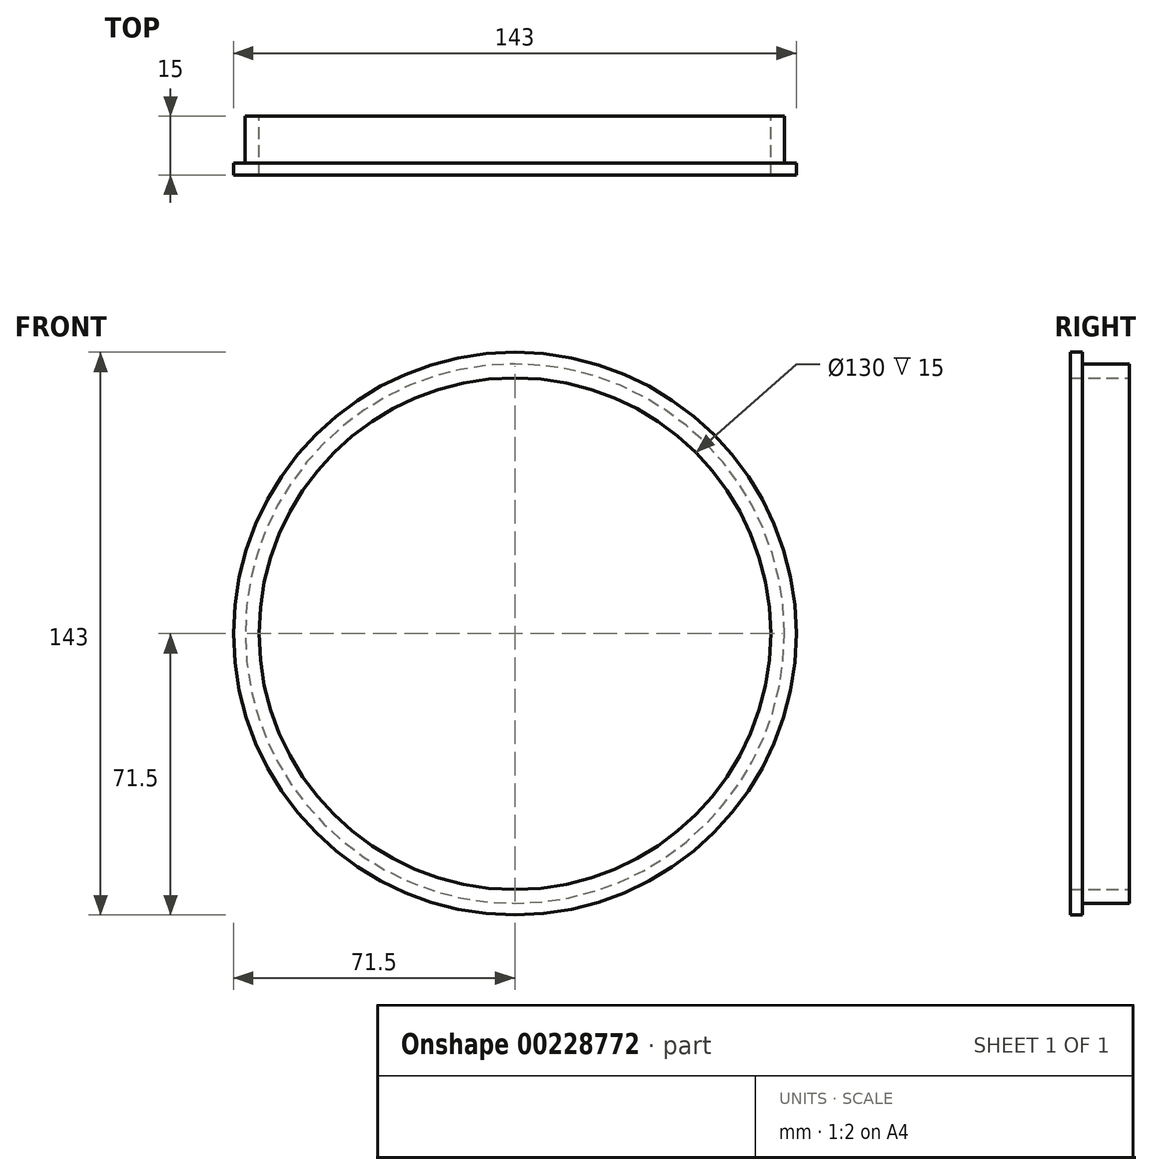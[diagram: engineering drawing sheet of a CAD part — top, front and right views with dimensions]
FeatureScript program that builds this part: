
annotation { "Feature Type Name" : "Feature", "Feature Type Description" : "" }
export const myFeature = defineFeature(function(context is Context, id is Id, definition is map)
    precondition{}
    {
        {
            var Q0;
            Q0=qCreatedBy(makeId("Top.planeOp"),FACE);
            var sketch = newSketch(context, id + "F0", { "sketchPlane" : qUnion([Q0])});
            skLineSegment(sketch, "E0", {"start": v(71.5, 0) * mm, "end": v(65, 0) * mm});
            skLineSegment(sketch, "E1", {"start": v(65, 0) * mm, "end": v(65, 15) * mm});
            skLineSegment(sketch, "E2", {"start": v(65, 15) * mm, "end": v(68.5, 15) * mm});
            skLineSegment(sketch, "E3", {"start": v(68.5, 15) * mm, "end": v(68.5, 3) * mm});
            skLineSegment(sketch, "E4", {"start": v(68.5, 3) * mm, "end": v(71.5, 3) * mm});
            skLineSegment(sketch, "E5", {"start": v(71.5, 3) * mm, "end": v(71.5, 0) * mm});
            skLineSegment(sketch, "E6", {"start": v(0, 20.25) * mm, "end": v(0, -17.86) * mm, "construction": true});
            skSolve(sketch);
        }
        {
            var Q0;
            Q0 = qSketchRegion(id + "F0", true);
            var Q1;
            Q1=sQuery(id+"F0.wireOp",EDGE,"E6");
            revolve(context, id + "F1", {"entities" : qUnion([Q0]), "axis" : qUnion([Q1]), "revolveType" : RevolveType.FULL});
        }
    });
